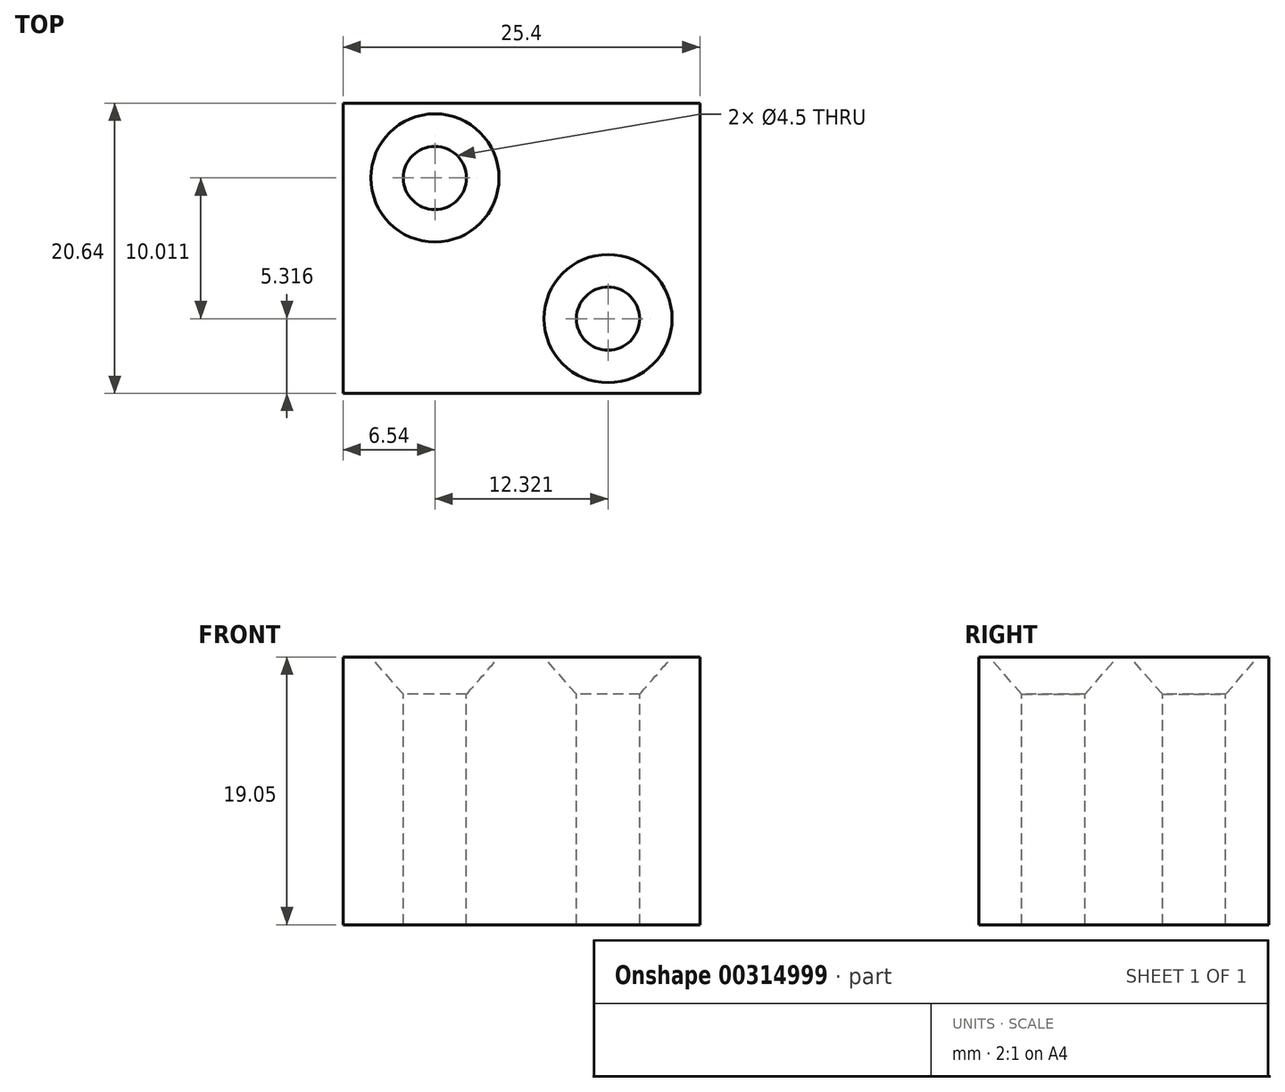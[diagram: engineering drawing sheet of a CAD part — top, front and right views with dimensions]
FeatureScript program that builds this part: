
annotation { "Feature Type Name" : "Feature", "Feature Type Description" : "" }
export const myFeature = defineFeature(function(context is Context, id is Id, definition is map)
    precondition{}
    {
        {
            var Q0;
            Q0=qCreatedBy(makeId("Top.planeOp"),FACE);
            var sketch = newSketch(context, id + "F0", { "sketchPlane" : qUnion([Q0])});
            skLineSegment(sketch, "E0.bottom", {"start": v(0, 0) * mm, "end": v(25.4, 0) * mm});
            skLineSegment(sketch, "E0.top", {"start": v(0, -20.64) * mm, "end": v(25.4, -20.64) * mm});
            skLineSegment(sketch, "E0.left", {"start": v(0, 0) * mm, "end": v(0, -20.64) * mm});
            skLineSegment(sketch, "E0.right", {"start": v(25.4, 0) * mm, "end": v(25.4, -20.64) * mm});
            skLineSegment(sketch, "E1", {"start": v(12.7, 0) * mm, "end": v(12.7, -20.64) * mm, "construction": true});
            skLineSegment(sketch, "E2", {"start": v(12.7, -20.64) * mm, "end": v(0, -10.32) * mm, "construction": true});
            skLineSegment(sketch, "E3", {"start": v(0, -10.32) * mm, "end": v(25.4, -10.32) * mm, "construction": true});
            skPoint(sketch, "E4", {"position": v(12.7, -10.32) * mm});
            skSolve(sketch);
        }
        {
            var Q0;
            Q0 = qSketchRegion(id + "F0", true);
            extrude(context, id + "F1", {"entities" : qUnion([Q0]), "depth" : 19.05 * mm});
        }
        {
            var Q0;
            Q0=makeQuery(id+"F1.opExtrude","CAP_FACE",FACE,{"disambiguationData":[OSD([sQuery(id+"F0.wireOp",EDGE,"E0.bottom"),sQuery(id+"F0.wireOp",EDGE,"E0.top"),sQuery(id+"F0.wireOp",EDGE,"E0.left"),sQuery(id+"F0.wireOp",EDGE,"E0.right")])],"isStart":false});
            var sketch = newSketch(context, id + "F2", { "sketchPlane" : qUnion([Q0])});
            skPoint(sketch, "E5.0", {"position": v(12.7, -10.32) * mm});
            skSolve(sketch);
        }
        {
            var Q0;
            Q0=makeQuery(id+"F2.imprint","IMPRINT",FACE,{"disambiguationData":[TD([[makeQuery(id+"F2.imprint","IMPRINT",EDGE,{"derivedFrom":makeQuery(id+"F1.opExtrude","CAP_EDGE",EDGE,{"disambiguationData":[OSD([sQuery(id+"F0.wireOp",EDGE,"E0.bottom")])],"isStart":false})}),-1.0]])]});
            var sketch = newSketch(context, id + "F3", { "sketchPlane" : qUnion([Q0])});
            skLineSegment(sketch, "E6.0", {"start": v(0, 0) * mm, "end": v(25.4, 0) * mm});
            skPoint(sketch, "E6.1", {"position": v(25.4, -20.64) * mm});
            skLineSegment(sketch, "E6.2", {"start": v(25.4, 0) * mm, "end": v(25.4, -20.64) * mm});
            skPoint(sketch, "E6.3", {"position": v(0, 0) * mm});
            skPoint(sketch, "E6.4", {"position": v(0, -20.64) * mm});
            skLineSegment(sketch, "E6.5", {"start": v(0, 0) * mm, "end": v(0, -20.64) * mm});
            skLineSegment(sketch, "E6.6.0", {"start": v(0, 0) * mm, "end": v(0, -20.64) * mm});
            skLineSegment(sketch, "E6.6.1", {"start": v(0, -20.64) * mm, "end": v(25.4, -20.64) * mm});
            skLineSegment(sketch, "E6.6.2", {"start": v(25.4, -20.64) * mm, "end": v(25.4, 0) * mm});
            skLineSegment(sketch, "E6.6.3", {"start": v(25.4, 0) * mm, "end": v(0, 0) * mm});
            skLineSegment(sketch, "E6.7", {"start": v(0, -20.64) * mm, "end": v(25.4, -20.64) * mm});
            skLineSegment(sketch, "E6.8.0", {"start": v(25.4, 0) * mm, "end": v(0, 0) * mm});
            skLineSegment(sketch, "E6.8.1", {"start": v(0, 0) * mm, "end": v(0, -20.64) * mm});
            skLineSegment(sketch, "E6.8.2", {"start": v(0, -20.64) * mm, "end": v(25.4, -20.64) * mm});
            skLineSegment(sketch, "E6.8.3", {"start": v(25.4, -20.64) * mm, "end": v(25.4, 0) * mm});
            skPoint(sketch, "E6.9", {"position": v(25.4, 0) * mm});
            skPoint(sketch, "E6.10", {"position": v(12.7, -10.32) * mm});
            skLineSegment(sketch, "E7", {"start": v(0, 0) * mm, "end": v(25.4, -20.64) * mm});
            skPoint(sketch, "E8", {"position": v(6.54, -5.31) * mm});
            skPoint(sketch, "E9", {"position": v(18.86, -15.32) * mm});
            skLineSegment(sketch, "E10", {"start": v(0, 0) * mm, "end": v(6.54, -5.31) * mm, "construction": true});
            skLineSegment(sketch, "E11", {"start": v(18.86, -15.32) * mm, "end": v(25.4, -20.64) * mm, "construction": true});
            skSolve(sketch);
        }
        {
            var Q0;
            Q0=sQuery(id+"F3.wireOp",VERTEX,"E8");
            var Q1;
            Q1=sQuery(id+"F3.wireOp",VERTEX,"E9");
            var Q2;
            Q2=makeQuery(id+"F1.opExtrude","SWEPT_BODY",BODY,{"disambiguationData":[OSD([sQuery(id+"F0.wireOp",EDGE,"E0.bottom"),sQuery(id+"F0.wireOp",EDGE,"E0.top"),sQuery(id+"F0.wireOp",EDGE,"E0.left"),sQuery(id+"F0.wireOp",EDGE,"E0.right")])]});
            hole(context, id + "F4", {"style" : HoleStyle.C_SINK, "endStyle" : HoleEndStyle.THROUGH, "standardTappedOrClearance" : lookupTablePath({ "standard" : "ANSI", "fit" : "Normal (ASME)", "size" : "#8", "type" : "Clearance" }), "standardBlindInLast" : lookupTablePath({ "fit" : "Free", "standard" : "ANSI", "size" : "#8", "type" : "Clearance" }), "holeDiameter" : 4.5 * mm, "cSinkDiameter" : 9.12 * mm, "cSinkAngle" : 82 * degree, "tappedDepth" : 12.7 * mm, "tapClearance" : 3, "locations" : qUnion([Q0, Q1]), "scope" : qUnion([Q2])});
        }
    });
